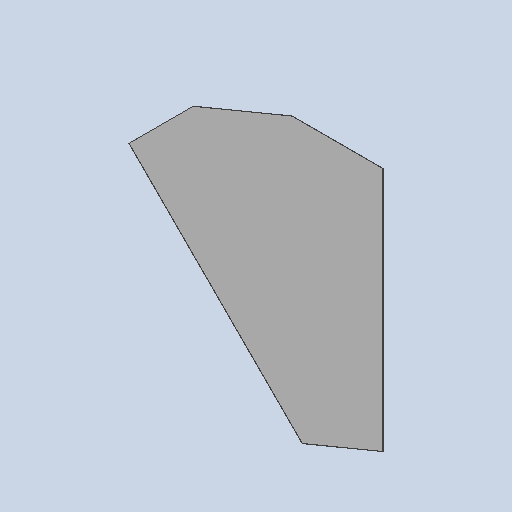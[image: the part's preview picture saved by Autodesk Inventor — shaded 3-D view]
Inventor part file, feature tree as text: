
AUTODESK INVENTOR PART (.ipt)
format: ipt  version: 2025 (Build 290162010, 162A)  size: 125,952 bytes
history: native  units: mm
features: extrude x2, sketch x2, pattern_linear x1
ambient origin geometry x8: Origin, YZ Plane, XZ Plane, XY Plane, X Axis, Y Axis, Z Axis, Center Point
bodies: Solid1 (feature_tree)
feature tree (5):
  extrude  "Extrusion1"  Depth=260.0mm
  extrude  "Extrusion5"  Depth=0.5mm TaperAngle=0.0deg
  pattern_linear  "Rectangular Pattern1"  Spacing1=15.0mm  [1 undecoded]
  sketch  "Sketch1"  dims[d0=513.0mm d2=260.0mm]
  sketch  "Sketch7"  dims[d3=635.0mm d5=0.5mm d6=0.0mm d10=15.0mm d54=8.0mm d55=8.0mm d56=5.0mm d57=5.0mm d58=0.0mm d59=0.0mm d60=300.0mm d62=25.0mm d63=300.0mm d65=25.0mm]
note: 1 required parameter value undecoded (feature->parameter linkage not recoverable at this tier; creation-order binding heuristic only, values carry confidence <= 0.55)
